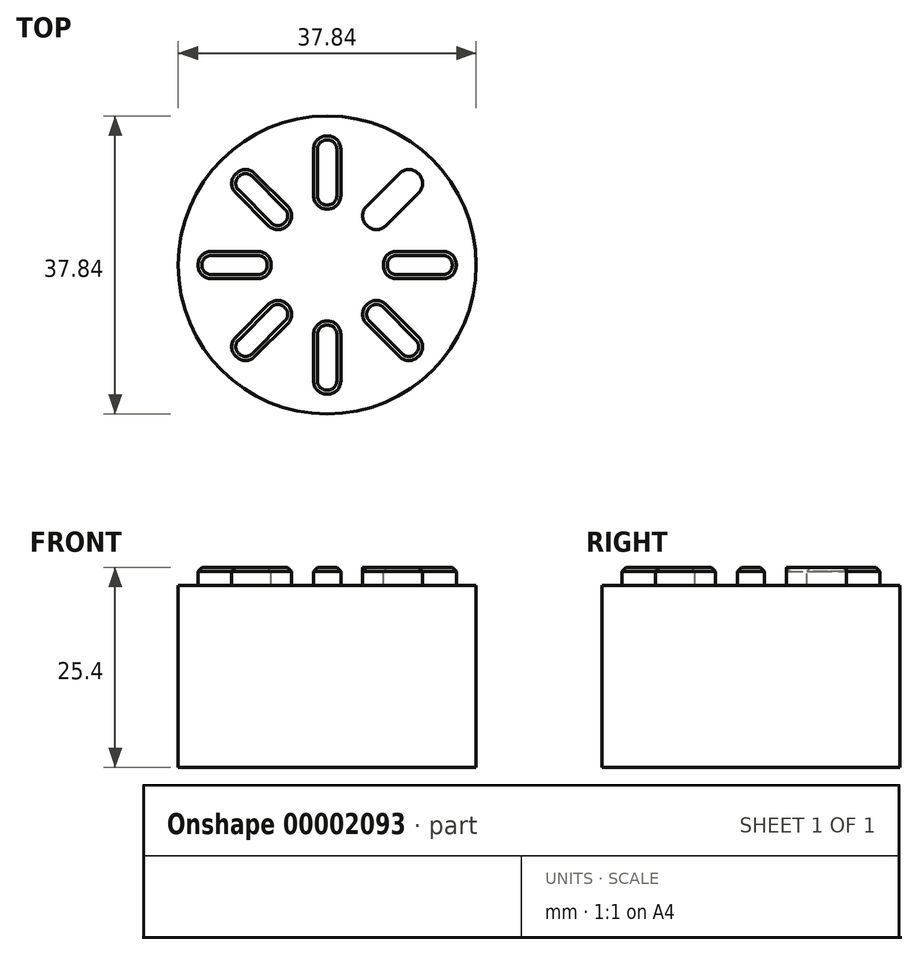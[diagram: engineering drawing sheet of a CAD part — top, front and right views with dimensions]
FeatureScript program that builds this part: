
annotation { "Feature Type Name" : "Feature", "Feature Type Description" : "" }
export const myFeature = defineFeature(function(context is Context, id is Id, definition is map)
    precondition{}
    {
        {
            var Q0;
            Q0=qCreatedBy(makeId("Top.planeOp"),FACE);
            var sketch = newSketch(context, id + "F0", { "sketchPlane" : qUnion([Q0])});
            skCircle(sketch, "E0", {"center": v(0, 0) * mm, "radius": 18.92 * mm});
            skCircle(sketch, "E1", {"center": v(0, 0) * mm, "radius": 4.58 * mm});
            skLineSegment(sketch, "E2", {"start": v(0, 7.12) * mm, "end": v(0, 16.4) * mm});
            skLineSegment(sketch, "E3", {"start": v(0, 16.4) * mm, "end": v(-0.08, 16.4) * mm});
            skLineSegment(sketch, "E4", {"start": v(-0.08, 7.12) * mm, "end": v(0, 7.12) * mm});
            skLineSegment(sketch, "E5", {"start": v(0.08, 16.4) * mm, "end": v(0, 16.4) * mm});
            skLineSegment(sketch, "E6", {"start": v(0, 7.12) * mm, "end": v(0.08, 7.12) * mm});
            skPoint(sketch, "E7.visualSharp", {"position": v(-1.73, 16.4) * mm});
            skArc(sketch, "E7.filletArc", {"start": v(-0.08, 16.4) * mm, "mid": v(-1.24, 15.91) * mm, "end": v(-1.73, 14.74) * mm});
            skPoint(sketch, "E8.visualSharp", {"position": v(1.73, 16.4) * mm});
            skArc(sketch, "E8.filletArc", {"start": v(1.73, 14.74) * mm, "mid": v(1.24, 15.91) * mm, "end": v(0.08, 16.4) * mm});
            skPoint(sketch, "E9.visualSharp", {"position": v(1.73, 7.12) * mm});
            skPoint(sketch, "E10.visualSharp", {"position": v(-1.73, 7.12) * mm});
            skLineSegment(sketch, "E11", {"start": v(-16.4, 0) * mm, "end": v(-16.4, 0.08) * mm});
            skLineSegment(sketch, "E12", {"start": v(-14.74, 1.73) * mm, "end": v(-8.78, 1.73) * mm});
            skLineSegment(sketch, "E13", {"start": v(-7.12, 0.08) * mm, "end": v(-7.12, 0) * mm});
            skLineSegment(sketch, "E14", {"start": v(-8.78, -1.73) * mm, "end": v(-14.74, -1.73) * mm});
            skLineSegment(sketch, "E15", {"start": v(-16.4, -0.08) * mm, "end": v(-16.4, 0) * mm});
            skLineSegment(sketch, "E16", {"start": v(-7.12, -0.08) * mm, "end": v(-7.12, 0) * mm});
            skPoint(sketch, "E17.visualSharp", {"position": v(-16.4, 1.73) * mm});
            skArc(sketch, "E17.filletArc", {"start": v(-14.74, 1.73) * mm, "mid": v(-15.91, 1.24) * mm, "end": v(-16.4, 0.08) * mm});
            skPoint(sketch, "E18.visualSharp", {"position": v(-16.4, -1.73) * mm});
            skArc(sketch, "E18.filletArc", {"start": v(-16.4, -0.08) * mm, "mid": v(-15.91, -1.24) * mm, "end": v(-14.74, -1.73) * mm});
            skPoint(sketch, "E19.visualSharp", {"position": v(-7.12, -1.73) * mm});
            skArc(sketch, "E19.filletArc", {"start": v(-8.78, -1.73) * mm, "mid": v(-7.6, -1.24) * mm, "end": v(-7.12, -0.08) * mm});
            skPoint(sketch, "E20.visualSharp", {"position": v(-7.12, 1.73) * mm});
            skArc(sketch, "E20.filletArc", {"start": v(-7.12, 0.08) * mm, "mid": v(-7.6, 1.24) * mm, "end": v(-8.78, 1.73) * mm});
            skLineSegment(sketch, "E21", {"start": v(7.12, 0) * mm, "end": v(16.4, 0) * mm});
            skLineSegment(sketch, "E22", {"start": v(16.4, 0) * mm, "end": v(16.4, 0.08) * mm});
            skLineSegment(sketch, "E23", {"start": v(14.74, 1.73) * mm, "end": v(8.78, 1.73) * mm});
            skLineSegment(sketch, "E24", {"start": v(7.12, 0.08) * mm, "end": v(7.12, 0) * mm});
            skLineSegment(sketch, "E25", {"start": v(7.12, 0) * mm, "end": v(7.12, -0.08) * mm});
            skLineSegment(sketch, "E26", {"start": v(8.78, -1.73) * mm, "end": v(14.74, -1.73) * mm});
            skLineSegment(sketch, "E27", {"start": v(16.4, -0.08) * mm, "end": v(16.4, 0) * mm});
            skPoint(sketch, "E28.visualSharp", {"position": v(7.12, 1.73) * mm});
            skArc(sketch, "E28.filletArc", {"start": v(8.78, 1.73) * mm, "mid": v(7.6, 1.24) * mm, "end": v(7.12, 0.08) * mm});
            skPoint(sketch, "E29.visualSharp", {"position": v(16.4, 1.73) * mm});
            skArc(sketch, "E29.filletArc", {"start": v(16.4, 0.08) * mm, "mid": v(15.91, 1.24) * mm, "end": v(14.74, 1.73) * mm});
            skPoint(sketch, "E30.visualSharp", {"position": v(16.4, -1.73) * mm});
            skArc(sketch, "E30.filletArc", {"start": v(14.74, -1.73) * mm, "mid": v(15.91, -1.24) * mm, "end": v(16.4, -0.08) * mm});
            skPoint(sketch, "E31.visualSharp", {"position": v(7.12, -1.73) * mm});
            skArc(sketch, "E31.filletArc", {"start": v(7.12, -0.08) * mm, "mid": v(7.6, -1.24) * mm, "end": v(8.78, -1.73) * mm});
            skLineSegment(sketch, "E32", {"start": v(-0.08, 7.12) * mm, "end": v(-0.08, 7.12) * mm});
            skLineSegment(sketch, "E33", {"start": v(0.08, 7.12) * mm, "end": v(0.08, 7.12) * mm});
            skLineSegment(sketch, "E34", {"start": v(-1.73, 14.74) * mm, "end": v(-1.73, 8.78) * mm});
            skLineSegment(sketch, "E35", {"start": v(1.73, 14.74) * mm, "end": v(1.73, 8.78) * mm});
            skArc(sketch, "E36.filletArc", {"start": v(-1.73, 8.78) * mm, "mid": v(-1.24, 7.6) * mm, "end": v(-0.08, 7.12) * mm});
            skArc(sketch, "E37.filletArc", {"start": v(0.08, 7.12) * mm, "mid": v(1.24, 7.6) * mm, "end": v(1.73, 8.78) * mm});
            skLineSegment(sketch, "E38", {"start": v(0, -7.12) * mm, "end": v(0, -16.4) * mm});
            skLineSegment(sketch, "E39", {"start": v(0, -16.4) * mm, "end": v(0.08, -16.4) * mm});
            skLineSegment(sketch, "E40", {"start": v(1.73, -14.74) * mm, "end": v(1.73, -8.78) * mm});
            skLineSegment(sketch, "E41", {"start": v(0.08, -7.12) * mm, "end": v(0, -7.12) * mm});
            skLineSegment(sketch, "E42", {"start": v(0, -7.12) * mm, "end": v(-0.08, -7.12) * mm});
            skLineSegment(sketch, "E43", {"start": v(-1.73, -8.78) * mm, "end": v(-1.73, -14.74) * mm});
            skLineSegment(sketch, "E44", {"start": v(-0.08, -16.4) * mm, "end": v(0, -16.4) * mm});
            skPoint(sketch, "E45.visualSharp", {"position": v(-1.73, -7.12) * mm});
            skArc(sketch, "E45.filletArc", {"start": v(-0.08, -7.12) * mm, "mid": v(-1.24, -7.6) * mm, "end": v(-1.73, -8.78) * mm});
            skPoint(sketch, "E46.visualSharp", {"position": v(1.73, -7.12) * mm});
            skArc(sketch, "E46.filletArc", {"start": v(1.73, -8.78) * mm, "mid": v(1.24, -7.6) * mm, "end": v(0.08, -7.12) * mm});
            skPoint(sketch, "E47.visualSharp", {"position": v(1.73, -16.4) * mm});
            skArc(sketch, "E47.filletArc", {"start": v(0.08, -16.4) * mm, "mid": v(1.24, -15.91) * mm, "end": v(1.73, -14.74) * mm});
            skPoint(sketch, "E48.visualSharp", {"position": v(-1.73, -16.4) * mm});
            skArc(sketch, "E48.filletArc", {"start": v(-1.73, -14.74) * mm, "mid": v(-1.24, -15.91) * mm, "end": v(-0.08, -16.4) * mm});
            skLineSegment(sketch, "E49", {"start": v(5.04, 5.04) * mm, "end": v(11.6, 11.6) * mm});
            skLineSegment(sketch, "E50", {"start": v(5.04, 5.04) * mm, "end": v(4.98, 5.1) * mm});
            skLineSegment(sketch, "E51", {"start": v(4.98, 7.43) * mm, "end": v(9.2, 11.65) * mm});
            skLineSegment(sketch, "E52", {"start": v(11.54, 11.65) * mm, "end": v(11.6, 11.6) * mm});
            skLineSegment(sketch, "E53", {"start": v(11.6, 11.6) * mm, "end": v(11.65, 11.54) * mm});
            skLineSegment(sketch, "E54", {"start": v(11.65, 9.2) * mm, "end": v(7.43, 4.98) * mm});
            skLineSegment(sketch, "E55", {"start": v(5.1, 4.98) * mm, "end": v(5.04, 5.04) * mm});
            skPoint(sketch, "E56.visualSharp", {"position": v(10.37, 12.81) * mm});
            skArc(sketch, "E56.filletArc", {"start": v(11.54, 11.65) * mm, "mid": v(10.37, 12.13) * mm, "end": v(9.2, 11.65) * mm});
            skPoint(sketch, "E57.visualSharp", {"position": v(12.81, 10.37) * mm});
            skArc(sketch, "E57.filletArc", {"start": v(11.65, 9.2) * mm, "mid": v(12.13, 10.37) * mm, "end": v(11.65, 11.54) * mm});
            skPoint(sketch, "E58.visualSharp", {"position": v(6.26, 3.82) * mm});
            skArc(sketch, "E58.filletArc", {"start": v(5.1, 4.98) * mm, "mid": v(6.26, 4.5) * mm, "end": v(7.43, 4.98) * mm});
            skPoint(sketch, "E59.visualSharp", {"position": v(3.82, 6.26) * mm});
            skArc(sketch, "E59.filletArc", {"start": v(4.98, 7.43) * mm, "mid": v(4.5, 6.26) * mm, "end": v(4.98, 5.1) * mm});
            skLineSegment(sketch, "E60", {"start": v(-5.04, 5.04) * mm, "end": v(-11.6, 11.6) * mm});
            skLineSegment(sketch, "E61", {"start": v(-5.04, 5.04) * mm, "end": v(-4.98, 5.1) * mm});
            skLineSegment(sketch, "E62", {"start": v(-4.98, 7.43) * mm, "end": v(-9.2, 11.65) * mm});
            skLineSegment(sketch, "E63", {"start": v(-11.54, 11.65) * mm, "end": v(-11.6, 11.6) * mm});
            skLineSegment(sketch, "E64", {"start": v(-11.6, 11.6) * mm, "end": v(-11.65, 11.54) * mm});
            skLineSegment(sketch, "E65", {"start": v(-11.65, 9.2) * mm, "end": v(-7.43, 4.98) * mm});
            skLineSegment(sketch, "E66", {"start": v(-5.1, 4.98) * mm, "end": v(-5.04, 5.04) * mm});
            skPoint(sketch, "E67.visualSharp", {"position": v(-10.37, 12.81) * mm});
            skArc(sketch, "E67.filletArc", {"start": v(-9.2, 11.65) * mm, "mid": v(-10.37, 12.13) * mm, "end": v(-11.54, 11.65) * mm});
            skPoint(sketch, "E68.visualSharp", {"position": v(-12.81, 10.37) * mm});
            skArc(sketch, "E68.filletArc", {"start": v(-11.65, 11.54) * mm, "mid": v(-12.13, 10.37) * mm, "end": v(-11.65, 9.2) * mm});
            skPoint(sketch, "E69.visualSharp", {"position": v(-3.82, 6.26) * mm});
            skArc(sketch, "E69.filletArc", {"start": v(-4.98, 5.1) * mm, "mid": v(-4.5, 6.26) * mm, "end": v(-4.98, 7.43) * mm});
            skPoint(sketch, "E70.visualSharp", {"position": v(-6.26, 3.82) * mm});
            skArc(sketch, "E70.filletArc", {"start": v(-7.43, 4.98) * mm, "mid": v(-6.26, 4.5) * mm, "end": v(-5.1, 4.98) * mm});
            skLineSegment(sketch, "E71", {"start": v(-5.04, -5.04) * mm, "end": v(-11.6, -11.6) * mm});
            skLineSegment(sketch, "E72", {"start": v(-5.04, -5.04) * mm, "end": v(-4.98, -5.1) * mm});
            skLineSegment(sketch, "E73", {"start": v(-4.98, -7.43) * mm, "end": v(-9.2, -11.65) * mm});
            skLineSegment(sketch, "E74", {"start": v(-11.54, -11.65) * mm, "end": v(-11.6, -11.6) * mm});
            skLineSegment(sketch, "E75", {"start": v(-11.6, -11.6) * mm, "end": v(-11.65, -11.54) * mm});
            skLineSegment(sketch, "E76", {"start": v(-11.65, -9.2) * mm, "end": v(-7.43, -4.98) * mm});
            skLineSegment(sketch, "E77", {"start": v(-5.1, -4.98) * mm, "end": v(-5.04, -5.04) * mm});
            skLineSegment(sketch, "E78", {"start": v(5.04, -5.04) * mm, "end": v(11.6, -11.6) * mm});
            skLineSegment(sketch, "E79", {"start": v(11.6, -11.6) * mm, "end": v(11.65, -11.54) * mm});
            skLineSegment(sketch, "E80", {"start": v(11.65, -9.2) * mm, "end": v(7.43, -4.98) * mm});
            skLineSegment(sketch, "E81", {"start": v(5.1, -4.98) * mm, "end": v(5.04, -5.04) * mm});
            skLineSegment(sketch, "E82", {"start": v(5.04, -5.04) * mm, "end": v(4.98, -5.1) * mm});
            skLineSegment(sketch, "E83", {"start": v(4.98, -7.43) * mm, "end": v(9.2, -11.65) * mm});
            skLineSegment(sketch, "E84", {"start": v(11.54, -11.65) * mm, "end": v(11.6, -11.6) * mm});
            skPoint(sketch, "E85.visualSharp", {"position": v(-6.26, -3.82) * mm});
            skArc(sketch, "E85.filletArc", {"start": v(-5.1, -4.98) * mm, "mid": v(-6.26, -4.5) * mm, "end": v(-7.43, -4.98) * mm});
            skPoint(sketch, "E86.visualSharp", {"position": v(-3.82, -6.26) * mm});
            skArc(sketch, "E86.filletArc", {"start": v(-4.98, -7.43) * mm, "mid": v(-4.5, -6.26) * mm, "end": v(-4.98, -5.1) * mm});
            skPoint(sketch, "E87.visualSharp", {"position": v(-10.37, -12.81) * mm});
            skArc(sketch, "E87.filletArc", {"start": v(-11.54, -11.65) * mm, "mid": v(-10.37, -12.13) * mm, "end": v(-9.2, -11.65) * mm});
            skPoint(sketch, "E88.visualSharp", {"position": v(-12.81, -10.37) * mm});
            skArc(sketch, "E88.filletArc", {"start": v(-11.65, -9.2) * mm, "mid": v(-12.13, -10.37) * mm, "end": v(-11.65, -11.54) * mm});
            skPoint(sketch, "E89.visualSharp", {"position": v(3.82, -6.26) * mm});
            skArc(sketch, "E89.filletArc", {"start": v(4.98, -5.1) * mm, "mid": v(4.5, -6.26) * mm, "end": v(4.98, -7.43) * mm});
            skPoint(sketch, "E90.visualSharp", {"position": v(12.81, -10.37) * mm});
            skArc(sketch, "E90.filletArc", {"start": v(11.65, -11.54) * mm, "mid": v(12.13, -10.37) * mm, "end": v(11.65, -9.2) * mm});
            skPoint(sketch, "E91.visualSharp", {"position": v(10.37, -12.81) * mm});
            skArc(sketch, "E91.filletArc", {"start": v(9.2, -11.65) * mm, "mid": v(10.37, -12.13) * mm, "end": v(11.54, -11.65) * mm});
            skPoint(sketch, "E92.visualSharp", {"position": v(6.26, -3.82) * mm});
            skArc(sketch, "E92.filletArc", {"start": v(7.43, -4.98) * mm, "mid": v(6.26, -4.5) * mm, "end": v(5.1, -4.98) * mm});
            skSolve(sketch);
        }
        {
            var Q0;
            Q0=qCreatedBy(makeId("Top.planeOp"),FACE);
            var sketch = newSketch(context, id + "F1", { "sketchPlane" : qUnion([Q0])});
            skCircle(sketch, "E93.0", {"center": v(0, 0) * mm, "radius": 18.92 * mm});
            skSolve(sketch);
        }
        {
            var Q0;
            Q0=makeQuery(id+"F1.imprint","IMPRINT",FACE,{"disambiguationData":[TD([[makeQuery(id+"F1.imprint","IMPRINT",EDGE,{"derivedFrom":sQuery(id+"F1.wireOp",EDGE,"E93.0")}),1.0]])]});
            extrude(context, id + "F2", {"entities" : qUnion([Q0]), "oppositeDirection" : true, "depth" : 25.4 * mm});
        }
        {
            var Q0;
            Q0 = qSketchRegion(id + "F0", true);
            extrude(context, id + "F3", {"entities" : qUnion([Q0]), "operationType" : NewBodyOperationType.REMOVE, "oppositeDirection" : true, "depth" : 2.3 * mm});
        }
        {
            var Q0;
            Q0=makeQuery(id+"F3.boolean.opBoolean","SPLIT",FACE,{"disambiguationData":[TD([makeQuery(id+"F3.opExtrude","SWEPT_FACE",FACE,{"disambiguationData":[OSD([sQuery(id+"F0.wireOp",EDGE,"E1")])]})])],"derivedFrom":makeQuery(id+"F2.opExtrude","CAP_FACE",FACE,{"disambiguationData":[OSD([sQuery(id+"F1.wireOp",EDGE,"E93.0")])],"isStart":true})});
            extrude(context, id + "F4", {"entities" : qUnion([Q0]), "operationType" : NewBodyOperationType.REMOVE, "oppositeDirection" : true, "depth" : 2.3 * mm});
        }
        {
            var Q0;
            Q0=makeQuery(id+"F3.boolean.opBoolean","COPY",EDGE,{"derivedFrom":makeQuery(id+"F3.opExtrude","CAP_EDGE",EDGE,{"disambiguationData":[OSD([sQuery(id+"F0.wireOp",EDGE,"E14")])],"isStart":true})});
            var Q1;
            Q1=makeQuery(id+"F3.boolean.opBoolean","COPY",EDGE,{"derivedFrom":makeQuery(id+"F3.opExtrude","CAP_EDGE",EDGE,{"disambiguationData":[OSD([sQuery(id+"F0.wireOp",EDGE,"E76")])],"isStart":true})});
            var Q2;
            Q2=makeQuery(id+"F3.boolean.opBoolean","COPY",EDGE,{"derivedFrom":makeQuery(id+"F3.opExtrude","CAP_EDGE",EDGE,{"disambiguationData":[OSD([sQuery(id+"F0.wireOp",EDGE,"E43")])],"isStart":true})});
            var Q3;
            Q3=makeQuery(id+"F3.boolean.opBoolean","COPY",EDGE,{"derivedFrom":makeQuery(id+"F3.opExtrude","CAP_EDGE",EDGE,{"disambiguationData":[OSD([sQuery(id+"F0.wireOp",EDGE,"E83")])],"isStart":true})});
            var Q4;
            Q4=makeQuery(id+"F3.boolean.opBoolean","COPY",EDGE,{"derivedFrom":makeQuery(id+"F3.opExtrude","CAP_EDGE",EDGE,{"disambiguationData":[OSD([sQuery(id+"F0.wireOp",EDGE,"E26")])],"isStart":true})});
            var Q5;
            Q5=makeQuery(id+"F3.boolean.opBoolean","COPY",EDGE,{"derivedFrom":makeQuery(id+"F3.opExtrude","CAP_EDGE",EDGE,{"disambiguationData":[OSD([sQuery(id+"F0.wireOp",EDGE,"E54")])],"isStart":true})});
            var Q6;
            Q6=makeQuery(id+"F3.boolean.opBoolean","COPY",EDGE,{"derivedFrom":makeQuery(id+"F3.opExtrude","CAP_EDGE",EDGE,{"disambiguationData":[OSD([sQuery(id+"F0.wireOp",EDGE,"E35")])],"isStart":true})});
            var Q7;
            Q7=makeQuery(id+"F3.boolean.opBoolean","COPY",EDGE,{"derivedFrom":makeQuery(id+"F3.opExtrude","CAP_EDGE",EDGE,{"disambiguationData":[OSD([sQuery(id+"F0.wireOp",EDGE,"E62")])],"isStart":true})});
            chamfer(context, id + "F5", {"entities" : qUnion([Q0, Q1, Q2, Q3, Q4, Q5, Q6, Q7]), "width" : 0.5 * mm, "tangentPropagation" : true});
        }
    });
